# Revit family: RBA4601-061
name_source: partatom
category: Plumbing Fixtures
units: mm (PartAtom-declared; Revit-internal decimal feet)

## family parameters
Always vertical = Yes
Cut with Voids When Loaded = No
Part Type = Normal
Room Calculation Point = No
Round Connector Dimension = Use Diameter
Shared = No
Work Plane-Based = No

## types (3) — shared parameters
CW Connection = Yes
Description = Raffaello Shower T-Rail
Distance Away from Toilet (default) = 1090 mm  [stored 3.57612 ft]
Distance Away from Wall (default) = 100 mm  [stored 0.328084 ft]
HW Connection = Yes
Manufacturer = RBA Group
Modified Issue = 20180813.01
OFFSET = 1000 mm  [stored 3.28084 ft]
URL = http://www.rba.com.au
Vent Connection = Yes
Waste Connection = Yes
zero-valued in all types: Default Elevation

## per-type parameters (varying)
| type | Materials and Finishes |
| RBA4601-061 | Stainless Steel / White Antibacterial Finish |
| RBA4601-068 | Stainless Steel / Matte Black Antibacterial Finish |
| RBA4601-069 | Stainless Steel / Bright Finish |

note: column(s) folded — value = type name in every type: Model

note: [stored X ft] marks values corroborated as IEEE doubles in the binary element streams (Revit-internal decimal feet)

## geometry (parser evidence)
native form markers: Blend x4, Sweep x3
no freeform markers — native parametric forms only
